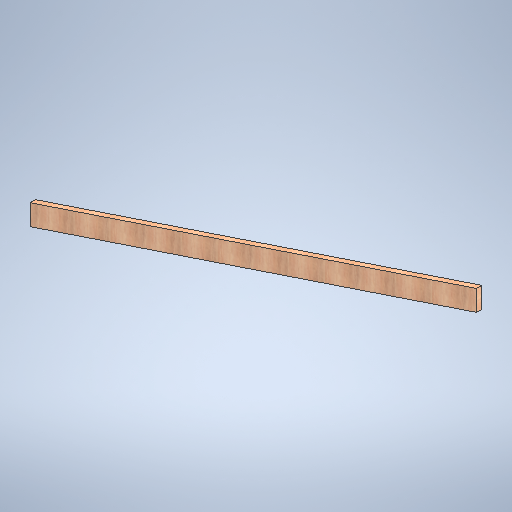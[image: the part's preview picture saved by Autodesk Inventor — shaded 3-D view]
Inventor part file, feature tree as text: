
AUTODESK INVENTOR PART (.ipt)
format: ipt  version: 2025 (Build 290162010, 162A)  size: 275,456 bytes
history: native  units: in
note: dims shown in document units (in); Inventor stores cm internally (conversion verified against a paired STEP export)
features: extrude x1, sketch x1
ambient origin geometry x8: Origin, YZ Plane, XZ Plane, XY Plane, X Axis, Y Axis, Z Axis, Center Point
bodies: Solid1 (feature_tree)
feature tree (2):
  extrude  "Extrusion1"  Depth=5.5in
  sketch  "Sketch1"  dims[d1=125.0in d4=5.5in d5=128.5in d6=42.875in d7=1.5in d8=0.0in]
